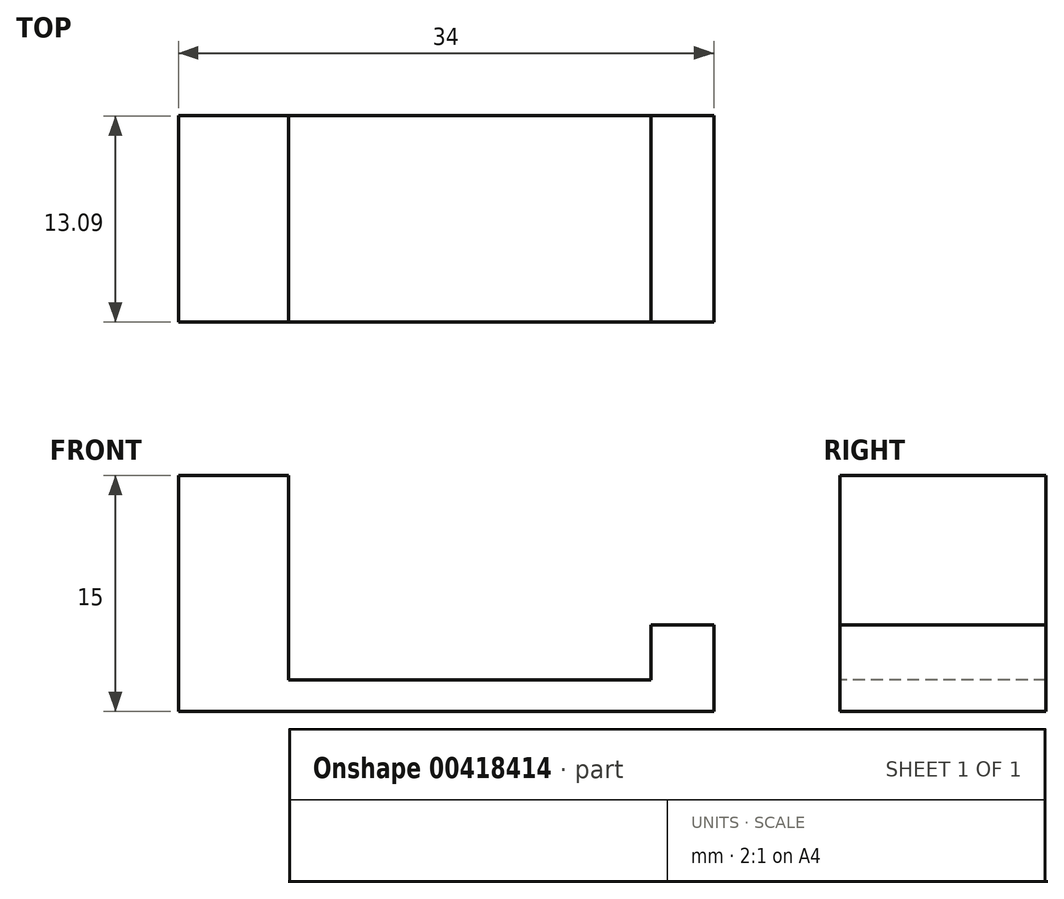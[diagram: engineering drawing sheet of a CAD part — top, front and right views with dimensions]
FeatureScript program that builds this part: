
annotation { "Feature Type Name" : "Feature", "Feature Type Description" : "" }
export const myFeature = defineFeature(function(context is Context, id is Id, definition is map)
    precondition{}
    {
        {
            var Q0;
            Q0=qCreatedBy(makeId("Top.planeOp"),FACE);
            var sketch = newSketch(context, id + "F0", { "sketchPlane" : qUnion([Q0])});
            skLineSegment(sketch, "E0.bottom", {"start": v(-30, 13.1) * mm, "end": v(-23, 13.1) * mm});
            skLineSegment(sketch, "E0.top", {"start": v(-30, 0) * mm, "end": v(-23, 0) * mm});
            skLineSegment(sketch, "E0.left", {"start": v(-30, 13.1) * mm, "end": v(-30, 0) * mm});
            skLineSegment(sketch, "E0.right", {"start": v(-23, 13.1) * mm, "end": v(-23, 0) * mm});
            skLineSegment(sketch, "E1.bottom", {"start": v(-23, 13.1) * mm, "end": v(0, 13.1) * mm});
            skLineSegment(sketch, "E1.top", {"start": v(-23, 0) * mm, "end": v(0, 0) * mm});
            skLineSegment(sketch, "E1.right", {"start": v(0, 13.1) * mm, "end": v(0, 0) * mm});
            skLineSegment(sketch, "E2.bottom", {"start": v(0, 13.1) * mm, "end": v(4, 13.1) * mm});
            skLineSegment(sketch, "E2.top", {"start": v(0, 0) * mm, "end": v(4, 0) * mm});
            skLineSegment(sketch, "E2.right", {"start": v(4, 13.1) * mm, "end": v(4, 0) * mm});
            skSolve(sketch);
        }
        {
            var Q0;
            Q0=makeQuery(id+"F0.imprint","IMPRINT",FACE,{"disambiguationData":[TD([[makeQuery(id+"F0.imprint","IMPRINT",EDGE,{"derivedFrom":sQuery(id+"F0.wireOp",EDGE,"E0.bottom")}),-1.0]])]});
            extrude(context, id + "F1", {"entities" : qUnion([Q0]), "depth" : 15 * mm});
        }
        {
            var Q0;
            Q0=makeQuery(id+"F0.imprint","IMPRINT",FACE,{"disambiguationData":[TD([[makeQuery(id+"F0.imprint","IMPRINT",EDGE,{"derivedFrom":sQuery(id+"F0.wireOp",EDGE,"E1.bottom")}),-1.0]])]});
            extrude(context, id + "F2", {"entities" : qUnion([Q0]), "operationType" : NewBodyOperationType.ADD, "depth" : 2 * mm});
        }
        {
            var Q0;
            Q0=makeQuery(id+"F0.imprint","IMPRINT",FACE,{"disambiguationData":[TD([[makeQuery(id+"F0.imprint","IMPRINT",EDGE,{"derivedFrom":sQuery(id+"F0.wireOp",EDGE,"E2.bottom")}),-1.0]])]});
            extrude(context, id + "F3", {"entities" : qUnion([Q0]), "operationType" : NewBodyOperationType.ADD, "depth" : 5.5 * mm});
        }
    });
